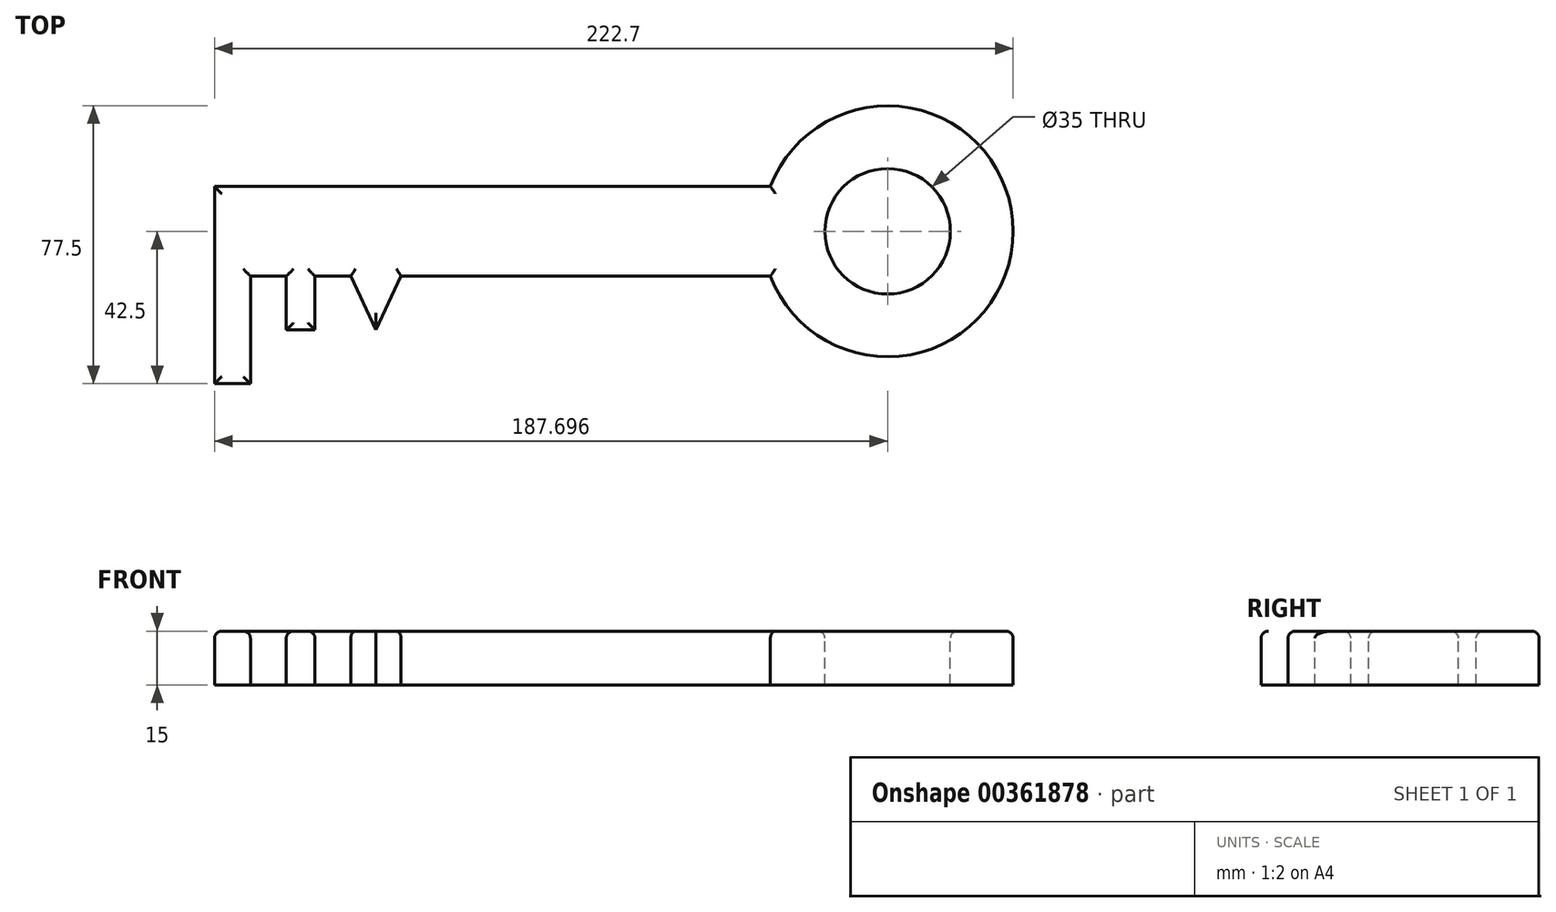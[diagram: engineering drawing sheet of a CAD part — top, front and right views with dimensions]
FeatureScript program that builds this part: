
annotation { "Feature Type Name" : "Feature", "Feature Type Description" : "" }
export const myFeature = defineFeature(function(context is Context, id is Id, definition is map)
    precondition{}
    {
        {
            var Q0;
            Q0=qCreatedBy(makeId("Top.planeOp"),FACE);
            var sketch = newSketch(context, id + "F0", { "sketchPlane" : qUnion([Q0])});
            skLineSegment(sketch, "E0.bottom", {"start": v(-78.53, 25) * mm, "end": v(76.47, 25) * mm});
            skLineSegment(sketch, "E0.top", {"start": v(-68.53, 0) * mm, "end": v(-58.53, 0) * mm});
            skLineSegment(sketch, "E0.left", {"start": v(-78.53, 25) * mm, "end": v(-78.53, 0) * mm});
            skLineSegment(sketch, "E1.top", {"start": v(-78.53, -30) * mm, "end": v(-68.53, -30) * mm});
            skLineSegment(sketch, "E1.left", {"start": v(-78.53, 0) * mm, "end": v(-78.53, -30) * mm});
            skLineSegment(sketch, "E1.right", {"start": v(-68.53, 0) * mm, "end": v(-68.53, -30) * mm});
            skLineSegment(sketch, "E2.top", {"start": v(-58.53, -15) * mm, "end": v(-50.53, -15) * mm});
            skLineSegment(sketch, "E2.left", {"start": v(-58.53, 0) * mm, "end": v(-58.53, -15) * mm});
            skLineSegment(sketch, "E2.right", {"start": v(-50.53, 0) * mm, "end": v(-50.53, -15) * mm});
            skPoint(sketch, "E3", {"position": v(-40.53, 0) * mm});
            skPoint(sketch, "E4", {"position": v(-26.53, 0) * mm});
            skPoint(sketch, "E5", {"position": v(-33.53, -15) * mm});
            skLineSegment(sketch, "E6", {"start": v(-40.53, 0) * mm, "end": v(-33.53, -15) * mm});
            skLineSegment(sketch, "E7", {"start": v(-33.53, -15) * mm, "end": v(-26.53, 0) * mm});
            skArc(sketch, "E8", {"start": v(76.47, 0) * mm, "mid": v(144.17, 12.5) * mm, "end": v(76.47, 25) * mm});
            skCircle(sketch, "E9", {"center": v(109.17, 12.5) * mm, "radius": 17.5 * mm});
            skLineSegment(sketch, "E10", {"start": v(109.17, 12.5) * mm, "end": v(-78.53, 12.5) * mm, "construction": true});
            skLineSegment(sketch, "E11.trimOffspring", {"start": v(-50.53, 0) * mm, "end": v(-40.53, 0) * mm});
            skLineSegment(sketch, "E12.trimOffspring", {"start": v(-26.53, 0) * mm, "end": v(76.47, 0) * mm});
            skSolve(sketch);
        }
        {
            var Q0;
            Q0=makeQuery(id+"F0.imprint","IMPRINT",FACE,{"disambiguationData":[TD([[makeQuery(id+"F0.imprint","IMPRINT",EDGE,{"derivedFrom":sQuery(id+"F0.wireOp",EDGE,"E0.bottom")}),-1.0]])]});
            extrude(context, id + "F1", {"entities" : qUnion([Q0]), "oppositeDirection" : true, "depth" : 15 * mm});
        }
        {
            var Q0;
            Q0=makeQuery(id+"F1.opExtrude","CAP_FACE",FACE,{"disambiguationData":[OSD([sQuery(id+"F0.wireOp",EDGE,"E0.bottom"),sQuery(id+"F0.wireOp",EDGE,"E0.top"),sQuery(id+"F0.wireOp",EDGE,"E0.left"),sQuery(id+"F0.wireOp",EDGE,"E1.top"),sQuery(id+"F0.wireOp",EDGE,"E1.left"),sQuery(id+"F0.wireOp",EDGE,"E1.right"),sQuery(id+"F0.wireOp",EDGE,"E2.top"),sQuery(id+"F0.wireOp",EDGE,"E2.left"),sQuery(id+"F0.wireOp",EDGE,"E2.right"),sQuery(id+"F0.wireOp",EDGE,"E6"),sQuery(id+"F0.wireOp",EDGE,"E7"),sQuery(id+"F0.wireOp",EDGE,"E8"),sQuery(id+"F0.wireOp",EDGE,"E9"),sQuery(id+"F0.wireOp",EDGE,"E11.trimOffspring"),sQuery(id+"F0.wireOp",EDGE,"E12.trimOffspring")])],"isStart":true});
            fillet(context, id + "F2", {"entities" : qUnion([Q0]), "radius" : 2 * mm, "tangentPropagation" : true, "allowEdgeOverflow" : false});
        }
    });
